# Revit family: NBS_AndersonGECLtd_KtchnStrgUnits_WallCabinet
name_source: partatom
category: Casework
revit_build: Autodesk Revit 2017 (Build: 20160225_1515(x64)
units: mm (PartAtom-declared; Revit-internal decimal feet)

## family parameters
Cut with Voids When Loaded = No
Host = Face
Room Calculation Point = No
Shared = No

## types (6) — shared parameters
AssetType = Fixed
CabinetDepth = 360 mm  [stored 1.1811 ft]
CabinetDoorMaterial = NBS_Concept
CabinetDoorThickness = 20 mm  [stored 0.0656168 ft]
CabinetHeight = 720 mm  [stored 2.3622 ft]
CabinetMaterial = NBS_Concept
Category = Pr_40_30_78_45:Kitchen storage units
Core = Fire-retardant core for fire-sensitive areas
Default Elevation = 1400 mm  [stored 4.59318 ft]
Depth = 360 mm  [stored 1.1811 ft]
Description = Wall-hung stainless steel base cabinets suitable for many environments and offer good stability and sound absorption
DoorsEdges = Back-slope
DurationUnit = year
ExpectedLife = 30 years
Features = Multiple handles, size range available
Finish = Stainless steel
Form = Fixed wall cabinet
GlazingOptions = Clear, frosted, wired door with stainless steel frame
HandleOptions = Integral handle, excluding handle, back-slope edge
Height = 720 mm  [stored 2.3622 ft]
HingeHoleOptions = Standard hinges, non-standard hinges
IfcExportAs = IfcFurnitureType
IfcExportType = CABINET
IntegralAccessories = Key operated lock, excluding handle
IsBuiltIn = Yes
ManufacturerName = Anderson, GEC Ltd
ManufacturerURL = www.gecanderson.co.uk
Material = Stainless steel
ModelNumber = V81
ModelReference = Wall cabinet
Mounting = Wall-fixed with up to 100 mm clearance
NBSCertification = www.nationalbimlibrary.com/cert/zs3bibdq
NBSDescription = Kitchen storage units
NBSReference = 45-35-80/340
NominalDepth = 380 mm  [stored 1.24672 ft]
NominalHeight = 720 mm  [stored 2.3622 ft]
NominalLength = 100 mm  [stored 0.328084 ft]
ProductInformation = http://www.gecanderson.co.uk
Shape = Rectangle
Status = New
Style = Wall cabinet
SustainabilityPerformance = 100% Recyclable
Uniclass2015Code = Pr_40_30_78_45
Uniclass2015Title = Kitchen storage units
Uniclass2015Version = Products v1.11
Version = 1
WarrantyDurationUnit = year

## per-type parameters (varying)
| type | BIMObjectName | CabinetWidth | IsDoubleDoor | IsSingleDoor | Name | NominalWidth | Size | Width |
| 400x380mm | NBS_AndersonGECLtd_KitchenStorageUnits_WallCabinet-1Door_400x380mm | 400 mm | No | Yes | KitchenStorageUnits_WallCabinet_400x380mm_AndersonGECLtd | 400 mm | 400 x 380 x 720 mm | 400 mm |
| 500x380mm | NBS_AndersonGECLtd_KitchenStorageUnits_WallCabinet-1Door_500x380mm | 500 mm | No | Yes | KitchenStorageUnits_WallCabinet_500x380mm_AndersonGECLtd | 500 mm | 500 x 380 x 720 mm | 500 mm |
| 600x380mm | NBS_AndersonGECLtd_KitchenStorageUnits_WallCabinet-1Door_600x380mm | 600 mm | No | Yes | KitchenStorageUnits_WallCabinet_600x380mm_AndersonGECLtd | 600 mm | 600 x 380 x 720 mm | 600 mm |
| 800x380mm | NBS_AndersonGECLtd_KitchenStorageUnits_WallCabinet-2Door_800x380mm | 800 mm  [stored 2.62467 ft] | Yes | No | KitchenStorageUnits_WallCabinet_800x380mm_AndersonGECLtd | 800 mm  [stored 2.62467 ft] | 800 x 380 x 720 mm | 800 mm  [stored 2.62467 ft] |
| 1000x380mm | NBS_AndersonGECLtd_KitchenStorageUnits_WallCabinet-2Door_1000x380mm | 1000 mm  [stored 3.28084 ft] | Yes | No | KitchenStorageUnits_WallCabinet_1000x380mm_AndersonGECLtd | 1000 mm  [stored 3.28084 ft] | 1000 x 380 x 720 mm | 1000 mm  [stored 3.28084 ft] |
| 1200x380mm | NBS_AndersonGECLtd_KitchenStorageUnits_WallCabinet-2Door_1200x380mm | 1200 mm | Yes | No | KitchenStorageUnits_WallCabinet_1200x380mm_AndersonGECLtd | 1200 mm | 1200 x 380 x 720 mm | 1200 mm |

note: [stored X ft] marks values corroborated as IEEE doubles in the binary element streams (Revit-internal decimal feet)

## geometry (parser evidence)
native form markers: Sweep x2
no freeform markers — native parametric forms only
